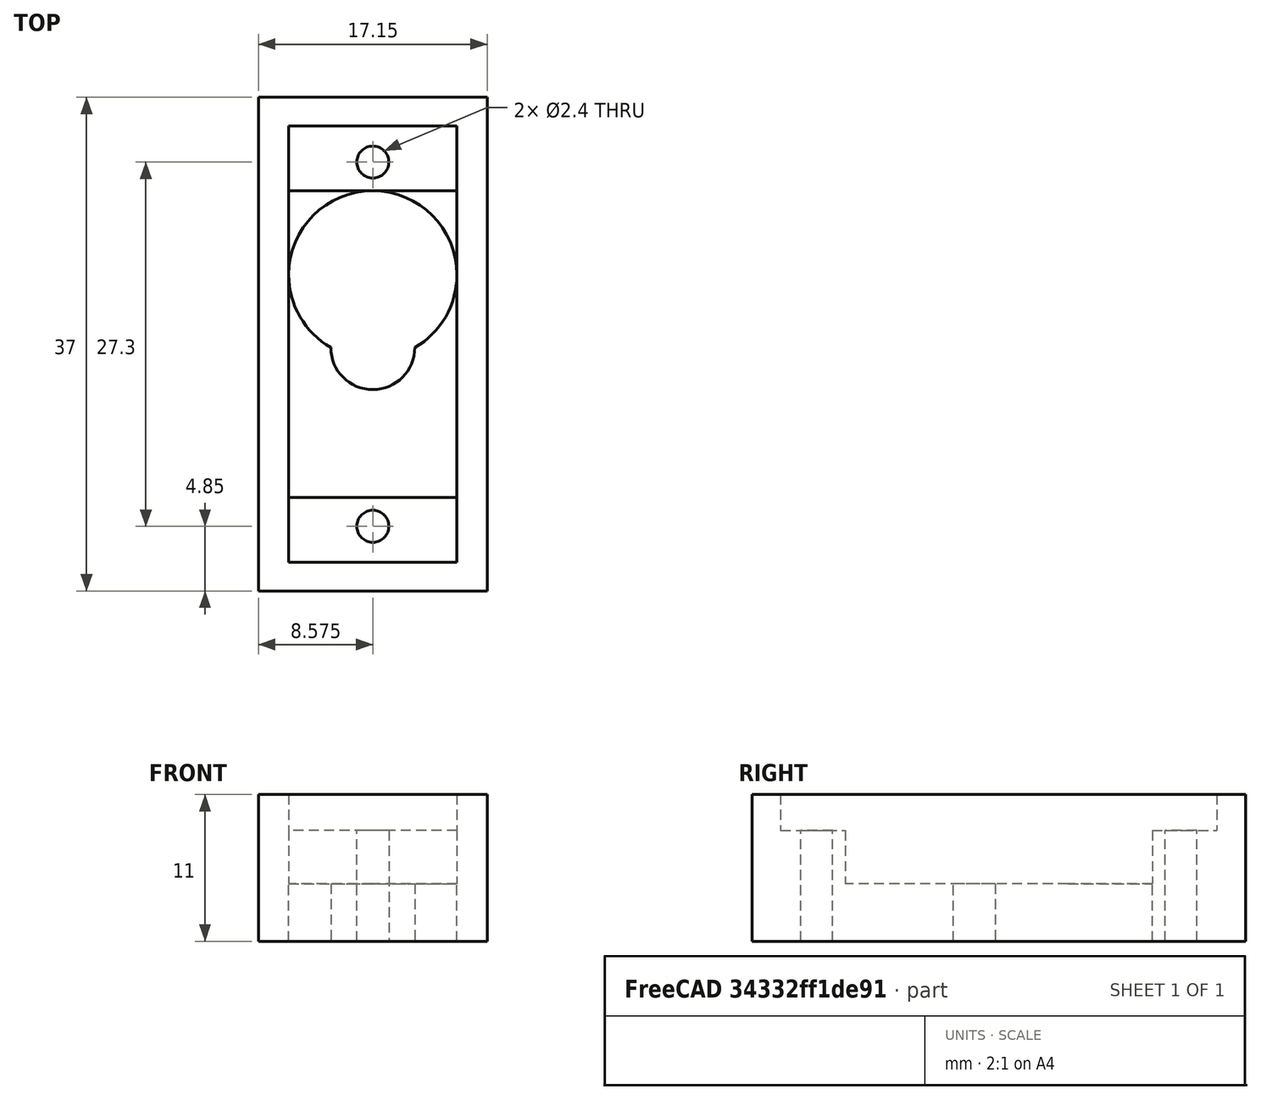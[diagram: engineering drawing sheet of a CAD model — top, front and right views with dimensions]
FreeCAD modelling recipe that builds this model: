
FCSTD DOCUMENT  (FreeCAD 0.19R24267 +148 (Git))
Label: Servohalterung
License: All rights reserved
LicenseURL: http://en.wikipedia.org/wiki/All_rights_reserved
objects: TechDraw::DrawViewDimension×18, Sketcher::SketchObject×5, PartDesign::Pocket×4, TechDraw::DrawProjGroupItem×4, PartDesign::Pad×1, PartDesign::Body×1, TechDraw::DrawSVGTemplate×1, TechDraw::DrawProjGroup×1, TechDraw::DrawPage×1
note: 16 computed .brp shape members not serialized (recipe doc carries the construction recipe); baked Part::Feature solids carry a one-line shape summary decoded from their .brp

FEATURE [Sketcher::SketchObject] Sketch
  FullyConstrained = true
  MapMode = 5
  Support = -> [XY_Plane]
  sketch-geometry (4):
    g0: LineSegment StartX=0 StartY=0 StartZ=0 EndX=17.15 EndY=0 EndZ=0
    g1: LineSegment StartX=17.15 StartY=0 StartZ=0 EndX=17.15 EndY=37 EndZ=0
    g2: LineSegment StartX=17.15 StartY=37 StartZ=0 EndX=0 EndY=37 EndZ=0
    g3: LineSegment StartX=0 StartY=37 StartZ=0 EndX=0 EndY=0 EndZ=0
  constraints (11):
    c: Coincident(g0,g1)
    c: Coincident(g1,g2)
    c: Coincident(g2,g3)
    c: Coincident(g3,g0)
    c: Horizontal(g0)
    c: Horizontal(g2)
    c: Vertical(g1)
    c: Vertical(g3)
    c: Coincident(g0,g-1)
    c: DistanceX(g2,g2) = 17.15
    c: DistanceY(g1,g1) = 37
FEATURE [PartDesign::Pad] Pad
  Direction = (1,1,1)
  Length = 11
  Length2 = 100
  Profile = -> Sketch
  Type = 0
FEATURE [Sketcher::SketchObject] Sketch001
  ExternalGeometry = -> [Pad]
  FullyConstrained = true
  MapMode = 5
  Placement = pos=(0,0,11) rot=(0,0,1;0rad)
  Support = -> [Pad]
  sketch-geometry (6):
    g0: LineSegment StartX=2.275 StartY=34.85 StartZ=0 EndX=14.875 EndY=34.85 EndZ=0
    g1: LineSegment StartX=14.875 StartY=34.85 StartZ=0 EndX=14.875 EndY=2.15 EndZ=0
    g2: LineSegment StartX=14.875 StartY=2.15 StartZ=0 EndX=2.275 EndY=2.15 EndZ=0
    g3: LineSegment StartX=2.275 StartY=2.15 StartZ=0 EndX=2.275 EndY=34.85 EndZ=0
    g4: LineSegment StartX=8.575 StartY=37 StartZ=0 EndX=8.575 EndY=0 EndZ=0
    g5: LineSegment StartX=0 StartY=18.5 StartZ=0 EndX=17.15 EndY=18.5 EndZ=0
  constraints (16):
    c: Coincident(g0,g1)
    c: Coincident(g1,g2)
    c: Coincident(g2,g3)
    c: Coincident(g3,g0)
    c: Horizontal(g2)
    c: Vertical(g3)
    c: PointOnObject(g4,g-1)
    c: Vertical(g4)
    c: PointOnObject(g5,g-2)
    c: Horizontal(g5)
    c: Symmetric(g-4,g-4,g5)
    c: Symmetric(g-3,g-4,g4)
    c: Symmetric(g0,g0,g4)
    c: Symmetric(g1,g0,g5)
    c: DistanceY(g1,g1) = 32.7
    c: DistanceX(g0,g0) = 12.6
FEATURE [PartDesign::Pocket] Pocket
  BaseFeature = -> Pad
  Length = 2.7
  Length2 = 100
  Profile = -> Sketch001
  Type = 0
FEATURE [Sketcher::SketchObject] Sketch002
  ExternalGeometry = -> [Pocket]
  FullyConstrained = true
  MapMode = 5
  Placement = pos=(0,0,8.3) rot=(0,0,1;0rad)
  Support = -> [Pocket]
  sketch-geometry (5):
    g0: LineSegment StartX=2.275 StartY=18.5 StartZ=0 EndX=14.875 EndY=18.5 EndZ=0
    g1: LineSegment StartX=2.275 StartY=7 StartZ=0 EndX=14.875 EndY=7 EndZ=0
    g2: LineSegment StartX=14.875 StartY=7 StartZ=0 EndX=14.875 EndY=30 EndZ=0
    g3: LineSegment StartX=14.875 StartY=30 StartZ=0 EndX=2.275 EndY=30 EndZ=0
    g4: LineSegment StartX=2.275 StartY=30 StartZ=0 EndX=2.275 EndY=7 EndZ=0
  constraints (14):
    c: PointOnObject(g0,g-3)
    c: Horizontal(g0)
    c: Symmetric(g-4,g-4,g0)
    c: Coincident(g1,g2)
    c: Coincident(g2,g3)
    c: Coincident(g3,g4)
    c: Coincident(g4,g1)
    c: Horizontal(g1)
    c: Horizontal(g3)
    c: Vertical(g2)
    c: Vertical(g4)
    c: PointOnObject(g2,g-4)
    c: Symmetric(g1,g3,g0)
    c: DistanceY(g1,g3) = 23
FEATURE [PartDesign::Pocket] Pocket001
  BaseFeature = -> Pocket
  Length = 4
  Length2 = 100
  Profile = -> Sketch002
  Type = 0
FEATURE [Sketcher::SketchObject] Sketch003
  ExternalGeometry = -> [Pocket001]
  FullyConstrained = true
  MapMode = 5
  Placement = pos=(0,0,4.3) rot=(0,0,1;0rad)
  Support = -> [Pocket001]
  sketch-geometry (6):
    g0: LineSegment StartX=8.575 StartY=30 StartZ=0 EndX=14.875 EndY=30 EndZ=0
    g1: LineSegment StartX=14.875 StartY=23.7 StartZ=0 EndX=14.875 EndY=30 EndZ=0
    g2: GeomPoint X=2.275 Y=23.7 Z=0
    g3: ArcOfCircle CenterX=8.575 CenterY=23.7 CenterZ=0 NormalX=0 NormalY=0 NormalZ=1 AngleXU=0 Radius=6.3 StartAngle=5.23599 EndAngle=10.472
    g4: ArcOfCircle CenterX=8.575 CenterY=18.244 CenterZ=0 NormalX=0 NormalY=0 NormalZ=1 AngleXU=0 Radius=3.15 StartAngle=3.14159 EndAngle=6.28319
    g5: LineSegment StartX=5.425 StartY=18.244 StartZ=0 EndX=11.725 EndY=18.244 EndZ=0
  constraints (19):
    c: PointOnObject(g1,g-5)
    c: Coincident(g1,g0)
    c: Equal(g1,g0)
    c: PointOnObject(g2,g-4)
    c: Horizontal(g1,g2)
    c: PointOnObject(g0,g3)
    c: PointOnObject(g1,g3)
    c: PointOnObject(g2,g3)
    c: Horizontal(g3,g3)
    c: Coincident(g4,g3)
    c: Coincident(g4,g3)
    c: Horizontal(g3,g4)
    c: Coincident(g5,g3)
    c: Coincident(g5,g3)
    c: Equal(g5,g0)
    c: Horizontal(g2,g3)
    c: Vertical(g3,g0)
    c: Horizontal(g0)
    c: DistanceY(g0,g-3) = 0
FEATURE [PartDesign::Pocket] Pocket002
  BaseFeature = -> Pocket001
  Length = 4.3
  Length2 = 100
  Profile = -> Sketch003
  Type = 0
FEATURE [Sketcher::SketchObject] Sketch004
  ExternalGeometry = -> [Pocket002]
  FullyConstrained = true
  MapMode = 5
  Placement = pos=(0,0,8.3) rot=(0,0,1;0rad)
  Support = -> [Pocket002]
  sketch-geometry (4):
    g0: Circle CenterX=8.575 CenterY=32.15 CenterZ=0 NormalX=0 NormalY=0 NormalZ=1 AngleXU=0 Radius=1.2
    g1: Circle CenterX=8.575 CenterY=4.85 CenterZ=0 NormalX=0 NormalY=0 NormalZ=1 AngleXU=0 Radius=1.2
    g2: LineSegment StartX=8.575 StartY=32.15 StartZ=0 EndX=8.575 EndY=30 EndZ=0
    g3: LineSegment StartX=8.575 StartY=4.85 StartZ=0 EndX=8.575 EndY=7 EndZ=0
  constraints (11):
    c: Equal(g1,g0)
    c: Vertical(g0,g-5)
    c: Vertical(g-5,g1)
    c: Coincident(g2,g0)
    c: Coincident(g2,g-5)
    c: Coincident(g3,g1)
    c: PointOnObject(g3,g-4)
    c: Vertical(g3)
    c: Equal(g3,g2)
    c: DistanceY(g2,g2) = 2.15
    c: Radius(g1) = 1.2
FEATURE [PartDesign::Pocket] Pocket003
  BaseFeature = -> Pocket002
  Length = 5
  Length2 = 100
  Profile = -> Sketch004
  Type = 1
FEATURE [PartDesign::Body] Body
  Group = -> [Sketch,Pad,Sketch001,Pocket,Sketch002,Pocket001,Sketch003,Pocket002,Sketch004,Pocket003]
  Origin = -> Origin
  Tip = -> Pocket003
FEATURE [TechDraw::DrawSVGTemplate] Template
  EditableTexts = Designed_by_Name=Designed by Name; Drawing_number=Drawing number; FC-Date=Date; FC-SC=Scale; FC-SH=Sheet; FC-Title=Title; Subtitle=Subtitle; Weight=Weight
  Height = 210
  Orientation = 1
  Width = 297
FEATURE [TechDraw::DrawProjGroupItem] ProjItem  label="Front"
  CoarseView = false
  Direction = (0,0,1)
  Focus = 100
  HardHidden = false
  IsoCount = 0
  IsoHidden = false
  IsoVisible = false
  LockPosition = true
  Perspective = false
  Rotation = 0
  RotationVector = (1,0,0)
  ScaleType = 2
  SeamHidden = false
  SeamVisible = true
  SmoothHidden = false
  SmoothVisible = true
  Source = -> [Body]
  Type = 0
  X = 0
  XDirection = (1,0,0)
  Y = 0
FEATURE [TechDraw::DrawProjGroupItem] ProjItem001  label="Left"
  CoarseView = false
  Direction = (-1,0,1e-16)
  Focus = 100
  HardHidden = false
  IsoCount = 0
  IsoHidden = false
  IsoVisible = false
  LockPosition = false
  Perspective = false
  Rotation = 0
  RotationVector = (1,0,0)
  ScaleType = 2
  SeamHidden = false
  SeamVisible = true
  SmoothHidden = false
  SmoothVisible = true
  Source = -> [Body]
  Type = 1
  X = 29.075
  XDirection = (1e-16,0,1)
  Y = 0
FEATURE [TechDraw::DrawProjGroupItem] ProjItem002  label="Rear"
  CoarseView = false
  Direction = (0,0,-1)
  Focus = 100
  HardHidden = false
  IsoCount = 0
  IsoHidden = false
  IsoVisible = false
  LockPosition = false
  Perspective = false
  Rotation = 0
  RotationVector = (1,0,0)
  ScaleType = 2
  SeamHidden = false
  SeamVisible = true
  SmoothHidden = false
  SmoothVisible = true
  Source = -> [Body]
  Type = 3
  X = 61.225
  XDirection = (-1,0,0)
  Y = 0
FEATURE [TechDraw::DrawProjGroupItem] ProjItem003  label="Bottom"
  CoarseView = false
  Direction = (0,-1,0)
  Focus = 100
  HardHidden = false
  IsoCount = 0
  IsoHidden = false
  IsoVisible = false
  LockPosition = false
  Perspective = false
  Rotation = 0
  RotationVector = (1,0,0)
  ScaleType = 2
  SeamHidden = false
  SeamVisible = true
  SmoothHidden = false
  SmoothVisible = true
  Source = -> [Body]
  Type = 5
  X = 0
  XDirection = (1,0,0)
  Y = 39
FEATURE [TechDraw::DrawProjGroup] ProjGroup
  Anchor = -> ProjItem
  AutoDistribute = true
  LockPosition = false
  ProjectionType = 0
  Rotation = 0
  ScaleType = 0
  Source = -> [Body]
  Views = -> [ProjItem,ProjItem001,ProjItem002,ProjItem003]
  X = 75.2581
  Y = 117.607
  spacingX = 15
  spacingY = 15
FEATURE [TechDraw::DrawViewDimension] Dimension
  Arbitrary = false
  ArbitraryTolerances = false
  EqualTolerance = true
  FormatSpec = R%.2f
  FormatSpecOverTolerance = %+.2f
  FormatSpecUnderTolerance = %+.2f
  Inverted = false
  LockPosition = false
  MeasureType = 1
  OverTolerance = 0
  References2D = -> [ProjItem]
  Rotation = 0
  ScaleType = 0
  TheoreticalExact = false
  Type = 4
  UnderTolerance = 0
  X = 2.89517
  Y = -21.7138
FEATURE [TechDraw::DrawViewDimension] Dimension001
  Arbitrary = false
  ArbitraryTolerances = false
  EqualTolerance = true
  FormatSpec = R%.2f
  FormatSpecOverTolerance = %+.2f
  FormatSpecUnderTolerance = %+.2f
  Inverted = false
  LockPosition = false
  MeasureType = 1
  OverTolerance = 0
  References2D = -> [ProjItem]
  Rotation = 0
  ScaleType = 0
  TheoreticalExact = false
  Type = 4
  UnderTolerance = 0
  X = 2.05075
  Y = 26.2978
FEATURE [TechDraw::DrawViewDimension] Dimension002
  Arbitrary = false
  ArbitraryTolerances = false
  EqualTolerance = true
  FormatSpec = R%.2f
  FormatSpecOverTolerance = %+.2f
  FormatSpecUnderTolerance = %+.2f
  Inverted = false
  LockPosition = false
  MeasureType = 1
  OverTolerance = 0
  References2D = -> [ProjItem]
  Rotation = 0
  ScaleType = 0
  TheoreticalExact = false
  Type = 4
  UnderTolerance = 0
  X = 16.1647
  Y = -6.63477
FEATURE [TechDraw::DrawViewDimension] Dimension003
  Arbitrary = false
  ArbitraryTolerances = false
  EqualTolerance = true
  FormatSpec = R%.2f
  FormatSpecOverTolerance = %+.2f
  FormatSpecUnderTolerance = %+.2f
  Inverted = false
  LockPosition = false
  MeasureType = 1
  OverTolerance = 0
  References2D = -> [ProjItem]
  Rotation = 0
  ScaleType = 0
  TheoreticalExact = false
  Type = 4
  UnderTolerance = 0
  X = 15.4409
  Y = 18.9393
FEATURE [TechDraw::DrawViewDimension] Dimension004
  Arbitrary = false
  ArbitraryTolerances = false
  EqualTolerance = true
  FormatSpec = %.2f
  FormatSpecOverTolerance = %+.2f
  FormatSpecUnderTolerance = %+.2f
  Inverted = false
  LockPosition = false
  MeasureType = 1
  OverTolerance = 0
  References2D = -> [ProjItem002]
  Rotation = 0
  ScaleType = 0
  TheoreticalExact = false
  Type = 1
  UnderTolerance = 0
  X = 0.241264
  Y = -34.5441
FEATURE [TechDraw::DrawViewDimension] Dimension005
  Arbitrary = false
  ArbitraryTolerances = false
  EqualTolerance = true
  FormatSpec = %.2f
  FormatSpecOverTolerance = %+.2f
  FormatSpecUnderTolerance = %+.2f
  Inverted = false
  LockPosition = false
  MeasureType = 1
  OverTolerance = 0
  References2D = -> [ProjItem002]
  Rotation = 0
  ScaleType = 0
  TheoreticalExact = false
  Type = 2
  UnderTolerance = 0
  X = 41.7489
  Y = -1.32695
FEATURE [TechDraw::DrawViewDimension] Dimension006
  Arbitrary = false
  ArbitraryTolerances = false
  EqualTolerance = true
  FormatSpec = %.2f
  FormatSpecOverTolerance = %+.2f
  FormatSpecUnderTolerance = %+.2f
  Inverted = false
  LockPosition = false
  MeasureType = 1
  OverTolerance = 0
  References2D = -> [ProjItem002]
  Rotation = 0
  ScaleType = 0
  TheoreticalExact = false
  Type = 2
  UnderTolerance = 0
  X = 23.2335
  Y = -9.61924
FEATURE [TechDraw::DrawViewDimension] Dimension007
  Arbitrary = false
  ArbitraryTolerances = false
  EqualTolerance = true
  FormatSpec = %.2f
  FormatSpecOverTolerance = %+.2f
  FormatSpecUnderTolerance = %+.2f
  Inverted = false
  LockPosition = false
  MeasureType = 1
  OverTolerance = 0
  References2D = -> [ProjItem002]
  Rotation = 0
  ScaleType = 0
  TheoreticalExact = false
  Type = 2
  UnderTolerance = 0
  X = 14.5444
  Y = -25.243
FEATURE [TechDraw::DrawViewDimension] Dimension008
  Arbitrary = false
  ArbitraryTolerances = false
  EqualTolerance = true
  FormatSpec = %.2f
  FormatSpecOverTolerance = %+.2f
  FormatSpecUnderTolerance = %+.2f
  Inverted = false
  LockPosition = false
  MeasureType = 1
  OverTolerance = 0
  References2D = -> [ProjItem002]
  Rotation = 0
  ScaleType = 0
  TheoreticalExact = false
  Type = 2
  UnderTolerance = 0
  X = 31.6742
  Y = -3.63132
FEATURE [TechDraw::DrawViewDimension] Dimension009
  Arbitrary = false
  ArbitraryTolerances = false
  EqualTolerance = true
  FormatSpec = %.2f
  FormatSpecOverTolerance = %+.2f
  FormatSpecUnderTolerance = %+.2f
  Inverted = false
  LockPosition = false
  MeasureType = 1
  OverTolerance = 0
  References2D = -> [ProjItem002]
  Rotation = 0
  ScaleType = 0
  TheoreticalExact = false
  Type = 1
  UnderTolerance = 0
  X = -16.2369
  Y = -23.8538
FEATURE [TechDraw::DrawViewDimension] Dimension010
  Arbitrary = false
  ArbitraryTolerances = false
  EqualTolerance = true
  FormatSpec = %.2f
  FormatSpecOverTolerance = %+.2f
  FormatSpecUnderTolerance = %+.2f
  Inverted = false
  LockPosition = false
  MeasureType = 1
  OverTolerance = 0
  References2D = -> [ProjItem002]
  Rotation = 0
  ScaleType = 0
  TheoreticalExact = false
  Type = 1
  UnderTolerance = 0
  X = -15.865
  Y = -16.4369
FEATURE [TechDraw::DrawViewDimension] Dimension011
  Arbitrary = false
  ArbitraryTolerances = false
  EqualTolerance = true
  FormatSpec = %.2f
  FormatSpecOverTolerance = %+.2f
  FormatSpecUnderTolerance = %+.2f
  Inverted = false
  LockPosition = false
  MeasureType = 1
  OverTolerance = 0
  References2D = -> [ProjItem]
  Rotation = 0
  ScaleType = 0
  TheoreticalExact = false
  Type = 1
  UnderTolerance = 0
  X = -19.3801
  Y = -29.3676
FEATURE [TechDraw::DrawViewDimension] Dimension012
  Arbitrary = false
  ArbitraryTolerances = false
  EqualTolerance = true
  FormatSpec = %.2f
  FormatSpecOverTolerance = %+.2f
  FormatSpecUnderTolerance = %+.2f
  Inverted = false
  LockPosition = false
  MeasureType = 1
  OverTolerance = 0
  References2D = -> [ProjItem]
  Rotation = 0
  ScaleType = 0
  TheoreticalExact = false
  Type = 2
  UnderTolerance = 0
  X = -15.0373
  Y = -22.3709
FEATURE [TechDraw::DrawViewDimension] Dimension013
  Arbitrary = false
  ArbitraryTolerances = false
  EqualTolerance = true
  FormatSpec = %.2f
  FormatSpecOverTolerance = %+.2f
  FormatSpecUnderTolerance = %+.2f
  Inverted = false
  LockPosition = false
  MeasureType = 1
  OverTolerance = 0
  References2D = -> [ProjItem]
  Rotation = 0
  ScaleType = 0
  TheoreticalExact = false
  Type = 2
  UnderTolerance = 0
  X = -22.5165
  Y = -22.9617
FEATURE [TechDraw::DrawViewDimension] Dimension014
  Arbitrary = false
  ArbitraryTolerances = false
  EqualTolerance = true
  FormatSpec = %.2f
  FormatSpecOverTolerance = %+.2f
  FormatSpecUnderTolerance = %+.2f
  Inverted = false
  LockPosition = false
  MeasureType = 1
  OverTolerance = 0
  References2D = -> [ProjItem]
  Rotation = 0
  ScaleType = 0
  TheoreticalExact = false
  Type = 2
  UnderTolerance = 0
  X = -30.7195
  Y = -7.37379
FEATURE [TechDraw::DrawViewDimension] Dimension015
  Arbitrary = false
  ArbitraryTolerances = false
  EqualTolerance = true
  FormatSpec = %.2f
  FormatSpecOverTolerance = %+.2f
  FormatSpecUnderTolerance = %+.2f
  Inverted = false
  LockPosition = false
  MeasureType = 1
  OverTolerance = 0
  References2D = -> [ProjItem]
  Rotation = 0
  ScaleType = 0
  TheoreticalExact = false
  Type = 2
  UnderTolerance = 0
  X = -39.2844
  Y = -0.725459
FEATURE [TechDraw::DrawViewDimension] Dimension016
  Arbitrary = false
  ArbitraryTolerances = false
  EqualTolerance = true
  FormatSpec = %.2f
  FormatSpecOverTolerance = %+.2f
  FormatSpecUnderTolerance = %+.2f
  Inverted = false
  LockPosition = false
  MeasureType = 1
  OverTolerance = 0
  References2D = -> [ProjItem]
  Rotation = 0
  ScaleType = 0
  TheoreticalExact = false
  Type = 2
  UnderTolerance = 0
  X = -48.5731
  Y = 1.21701
FEATURE [TechDraw::DrawViewDimension] Dimension017
  Arbitrary = false
  ArbitraryTolerances = false
  EqualTolerance = true
  FormatSpec = %.2f
  FormatSpecOverTolerance = %+.2f
  FormatSpecUnderTolerance = %+.2f
  Inverted = false
  LockPosition = false
  MeasureType = 1
  OverTolerance = 0
  References2D = -> [ProjItem001]
  Rotation = 0
  ScaleType = 0
  TheoreticalExact = false
  Type = 1
  UnderTolerance = 0
  X = -0.500286
  Y = -24.5034
FEATURE [TechDraw::DrawPage] Page
  KeepUpdated = true
  NextBalloonIndex = 1
  ProjectionType = 0
  Template = -> Template
  Views = -> [ProjGroup,Dimension,Dimension001,Dimension002,Dimension003,Dimension004,Dimension005,Dimension006,Dimension007,Dimension008,Dimension009,Dimension010,Dimension011,Dimension012,Dimension013,Dimension014,Dimension015,Dimension016,Dimension017]
